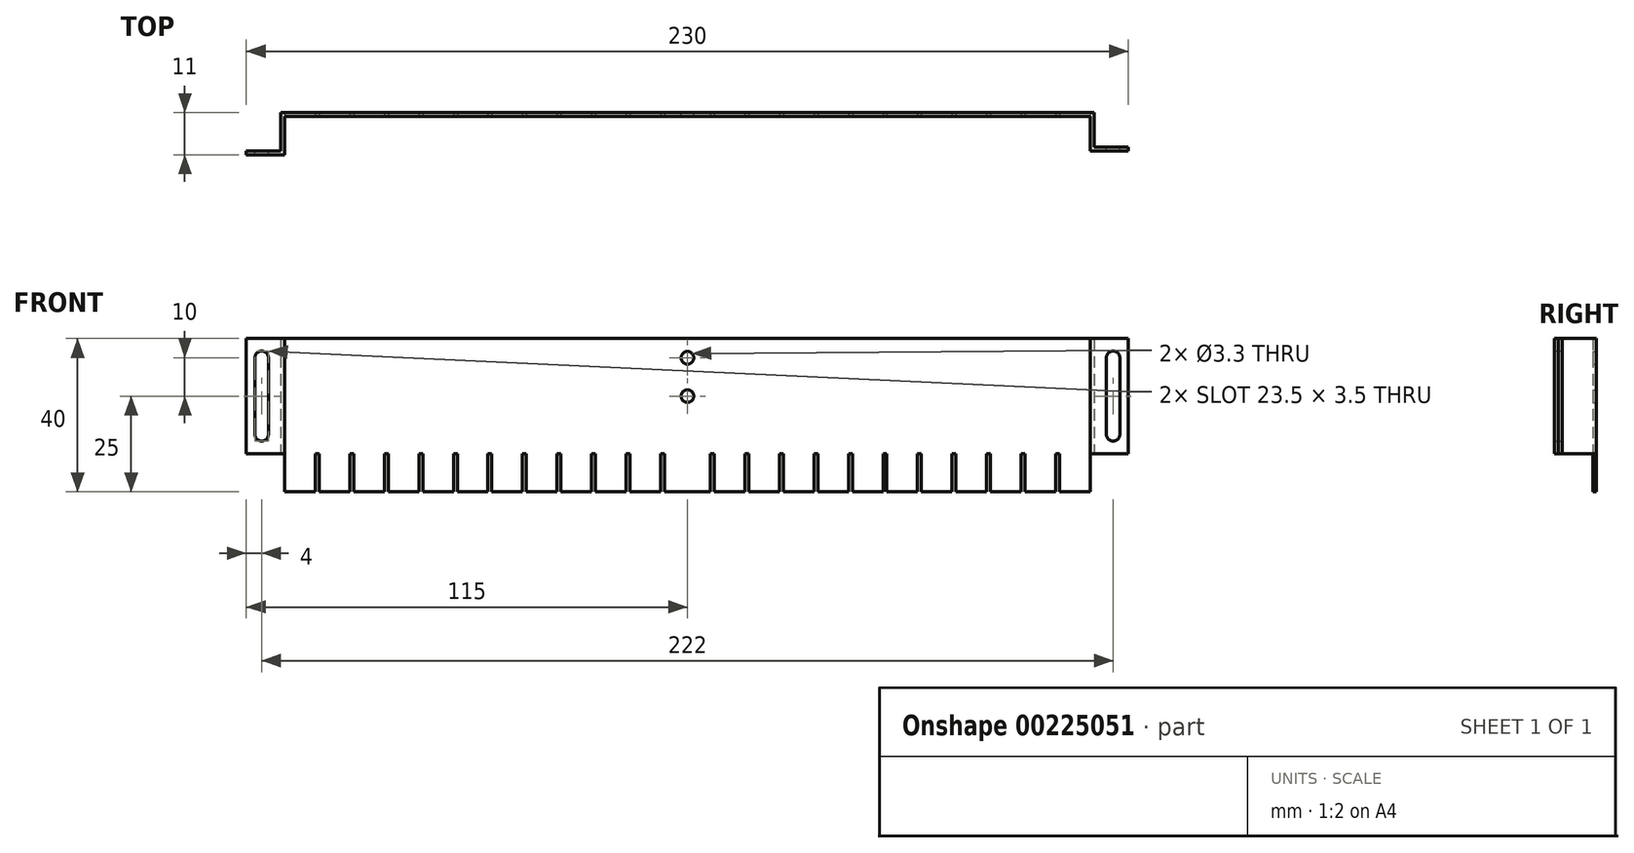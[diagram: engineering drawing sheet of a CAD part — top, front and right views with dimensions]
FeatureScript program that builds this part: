
annotation { "Feature Type Name" : "Feature", "Feature Type Description" : "" }
export const myFeature = defineFeature(function(context is Context, id is Id, definition is map)
    precondition{}
    {
        {
            var Q0;
            Q0=qCreatedBy(makeId("Top.planeOp"),FACE);
            var sketch = newSketch(context, id + "F0", { "sketchPlane" : qUnion([Q0])});
            skLineSegment(sketch, "E0", {"start": v(-115, -1) * mm, "end": v(-105, -1) * mm});
            skLineSegment(sketch, "E1", {"start": v(-105, -1) * mm, "end": v(-105, 9) * mm});
            skLineSegment(sketch, "E2", {"start": v(-105, 9) * mm, "end": v(105, 9) * mm});
            skLineSegment(sketch, "E3", {"start": v(105, 9) * mm, "end": v(105, 0) * mm});
            skLineSegment(sketch, "E4", {"start": v(105, 0) * mm, "end": v(115, 0) * mm});
            skLineSegment(sketch, "E5", {"start": v(115, 0) * mm, "end": v(115, 1) * mm});
            skLineSegment(sketch, "E6", {"start": v(115, 1) * mm, "end": v(106, 1) * mm});
            skLineSegment(sketch, "E7", {"start": v(106, 1) * mm, "end": v(106, 10) * mm});
            skLineSegment(sketch, "E8", {"start": v(106, 10) * mm, "end": v(-106, 10) * mm});
            skLineSegment(sketch, "E9", {"start": v(-106, 10) * mm, "end": v(-106, 0) * mm});
            skLineSegment(sketch, "E10", {"start": v(-106, 0) * mm, "end": v(-115, 0) * mm});
            skLineSegment(sketch, "E11", {"start": v(-115, 0) * mm, "end": v(-115, -1) * mm});
            skSolve(sketch);
        }
        {
            var Q0;
            Q0=qSketchRegion(id+"F0",true);
            extrude(context, id + "F1", {"entities" : qUnion([Q0]), "depth" : 30 * mm});
        }
        {
            var Q0;
            Q0=makeQuery(id+"F1.opExtrude","SWEPT_FACE",FACE,{"disambiguationData":[OSD([sQuery(id+"F0.wireOp",EDGE,"E6")])]});
            var sketch = newSketch(context, id + "F2", { "sketchPlane" : qUnion([Q0])});
            skArc(sketch, "E12", {"start": v(-109.25, 25) * mm, "mid": v(-111, 26.75) * mm, "end": v(-112.75, 25) * mm});
            skArc(sketch, "E13", {"start": v(-112.75, 5) * mm, "mid": v(-111, 3.25) * mm, "end": v(-109.25, 5) * mm});
            skLineSegment(sketch, "E14", {"start": v(-112.75, 25) * mm, "end": v(-112.75, 5) * mm});
            skLineSegment(sketch, "E15", {"start": v(-109.25, 5) * mm, "end": v(-109.25, 25) * mm});
            skLineSegment(sketch, "E16.MirrorCS", {"start": v(109.25, 5) * mm, "end": v(109.25, 25) * mm});
            skLineSegment(sketch, "E17.MirrorCS", {"start": v(112.75, 25) * mm, "end": v(112.75, 5) * mm});
            skArc(sketch, "E18.MirrorCS", {"start": v(112.75, 5) * mm, "mid": v(111, 3.25) * mm, "end": v(109.25, 5) * mm});
            skArc(sketch, "E19.MirrorCS", {"start": v(109.25, 25) * mm, "mid": v(111, 26.75) * mm, "end": v(112.75, 25) * mm});
            skSolve(sketch);
        }
        {
            var Q0;
            Q0=qSketchRegion(id+"F2",true);
            extrude(context, id + "F3", {"entities" : qUnion([Q0]), "operationType" : NewBodyOperationType.REMOVE, "oppositeDirection" : true, "depth" : 25 * mm});
        }
        {
            var Q0;
            Q0=makeQuery(id+"F1.opExtrude","SWEPT_FACE",FACE,{"disambiguationData":[OSD([sQuery(id+"F0.wireOp",EDGE,"E2")])]});
            var sketch = newSketch(context, id + "F4", { "sketchPlane" : qUnion([Q0])});
            skLineSegment(sketch, "E20.bottom", {"start": v(-105, 0) * mm, "end": v(-97, 0) * mm});
            skLineSegment(sketch, "E20.top", {"start": v(-105, -10) * mm, "end": v(-97, -10) * mm});
            skLineSegment(sketch, "E20.left", {"start": v(-105, 0) * mm, "end": v(-105, -10) * mm});
            skLineSegment(sketch, "E20.right", {"start": v(-97, 0) * mm, "end": v(-97, -10) * mm});
            skLineSegment(sketch, "E21.1.0.0", {"start": v(-96, 0) * mm, "end": v(-88, 0) * mm});
            skLineSegment(sketch, "E21.1.0.1", {"start": v(-96, -10) * mm, "end": v(-88, -10) * mm});
            skLineSegment(sketch, "E21.1.0.2", {"start": v(-96, 0) * mm, "end": v(-96, -10) * mm});
            skLineSegment(sketch, "E21.1.0.3", {"start": v(-88, 0) * mm, "end": v(-88, -10) * mm});
            skLineSegment(sketch, "E21.2.0.0", {"start": v(-87, 0) * mm, "end": v(-79, 0) * mm});
            skLineSegment(sketch, "E21.2.0.1", {"start": v(-87, -10) * mm, "end": v(-79, -10) * mm});
            skLineSegment(sketch, "E21.2.0.2", {"start": v(-87, 0) * mm, "end": v(-87, -10) * mm});
            skLineSegment(sketch, "E21.2.0.3", {"start": v(-79, 0) * mm, "end": v(-79, -10) * mm});
            skLineSegment(sketch, "E21.3.0.0", {"start": v(-78, 0) * mm, "end": v(-70, 0) * mm});
            skLineSegment(sketch, "E21.3.0.1", {"start": v(-78, -10) * mm, "end": v(-70, -10) * mm});
            skLineSegment(sketch, "E21.3.0.2", {"start": v(-78, 0) * mm, "end": v(-78, -10) * mm});
            skLineSegment(sketch, "E21.3.0.3", {"start": v(-70, 0) * mm, "end": v(-70, -10) * mm});
            skLineSegment(sketch, "E21.4.0.0", {"start": v(-69, 0) * mm, "end": v(-61, 0) * mm});
            skLineSegment(sketch, "E21.4.0.1", {"start": v(-69, -10) * mm, "end": v(-61, -10) * mm});
            skLineSegment(sketch, "E21.4.0.2", {"start": v(-69, 0) * mm, "end": v(-69, -10) * mm});
            skLineSegment(sketch, "E21.4.0.3", {"start": v(-61, 0) * mm, "end": v(-61, -10) * mm});
            skLineSegment(sketch, "E21.5.0.0", {"start": v(-60, 0) * mm, "end": v(-52, 0) * mm});
            skLineSegment(sketch, "E21.5.0.1", {"start": v(-60, -10) * mm, "end": v(-52, -10) * mm});
            skLineSegment(sketch, "E21.5.0.2", {"start": v(-60, 0) * mm, "end": v(-60, -10) * mm});
            skLineSegment(sketch, "E21.5.0.3", {"start": v(-52, 0) * mm, "end": v(-52, -10) * mm});
            skLineSegment(sketch, "E21.direction1", {"start": v(-105, -10) * mm, "end": v(-96, -10) * mm, "construction": true});
            skLineSegment(sketch, "E22.0.6.0", {"start": v(-51, 0) * mm, "end": v(-43, 0) * mm});
            skLineSegment(sketch, "E22.3.6.0", {"start": v(-51, -10) * mm, "end": v(-43, -10) * mm});
            skLineSegment(sketch, "E22.6.6.0", {"start": v(-51, 0) * mm, "end": v(-51, -10) * mm});
            skLineSegment(sketch, "E22.9.6.0", {"start": v(-43, 0) * mm, "end": v(-43, -10) * mm});
            skLineSegment(sketch, "E22.0.7.0", {"start": v(-42, 0) * mm, "end": v(-34, 0) * mm});
            skLineSegment(sketch, "E22.3.7.0", {"start": v(-42, -10) * mm, "end": v(-34, -10) * mm});
            skLineSegment(sketch, "E22.6.7.0", {"start": v(-42, 0) * mm, "end": v(-42, -10) * mm});
            skLineSegment(sketch, "E22.9.7.0", {"start": v(-34, 0) * mm, "end": v(-34, -10) * mm});
            skLineSegment(sketch, "E22.0.8.0", {"start": v(-33, 0) * mm, "end": v(-25, 0) * mm});
            skLineSegment(sketch, "E22.3.8.0", {"start": v(-33, -10) * mm, "end": v(-25, -10) * mm});
            skLineSegment(sketch, "E22.6.8.0", {"start": v(-33, 0) * mm, "end": v(-33, -10) * mm});
            skLineSegment(sketch, "E22.9.8.0", {"start": v(-25, 0) * mm, "end": v(-25, -10) * mm});
            skLineSegment(sketch, "E22.0.9.0", {"start": v(-24, 0) * mm, "end": v(-16, 0) * mm});
            skLineSegment(sketch, "E22.3.9.0", {"start": v(-24, -10) * mm, "end": v(-16, -10) * mm});
            skLineSegment(sketch, "E22.6.9.0", {"start": v(-24, 0) * mm, "end": v(-24, -10) * mm});
            skLineSegment(sketch, "E22.9.9.0", {"start": v(-16, 0) * mm, "end": v(-16, -10) * mm});
            skLineSegment(sketch, "E23.0.10.0", {"start": v(-15, 0) * mm, "end": v(-7, 0) * mm});
            skLineSegment(sketch, "E23.3.10.0", {"start": v(-15, -10) * mm, "end": v(-7, -10) * mm});
            skLineSegment(sketch, "E23.6.10.0", {"start": v(-15, 0) * mm, "end": v(-15, -10) * mm});
            skLineSegment(sketch, "E23.9.10.0", {"start": v(-7, 0) * mm, "end": v(-7, -10) * mm});
            skPoint(sketch, "E24.oppositeSnap0", {"position": v(-100.5, -10) * mm});
            skLineSegment(sketch, "E24.bottom", {"start": v(105, 0) * mm, "end": v(97, 0) * mm});
            skLineSegment(sketch, "E24.top", {"start": v(105, -10) * mm, "end": v(97, -10) * mm});
            skLineSegment(sketch, "E24.left", {"start": v(105, 0) * mm, "end": v(105, -10) * mm});
            skLineSegment(sketch, "E24.right", {"start": v(97, 0) * mm, "end": v(97, -10) * mm});
            skLineSegment(sketch, "E25.1.0.0", {"start": v(96, -10) * mm, "end": v(88, -10) * mm});
            skLineSegment(sketch, "E25.1.0.1", {"start": v(96, 0) * mm, "end": v(88, 0) * mm});
            skLineSegment(sketch, "E25.1.0.2", {"start": v(88, 0) * mm, "end": v(88, -10) * mm});
            skLineSegment(sketch, "E25.1.0.3", {"start": v(96, 0) * mm, "end": v(96, -10) * mm});
            skLineSegment(sketch, "E25.2.0.0", {"start": v(87, -10) * mm, "end": v(79, -10) * mm});
            skLineSegment(sketch, "E25.2.0.1", {"start": v(87, 0) * mm, "end": v(79, 0) * mm});
            skLineSegment(sketch, "E25.2.0.2", {"start": v(79, 0) * mm, "end": v(79, -10) * mm});
            skLineSegment(sketch, "E25.2.0.3", {"start": v(87, 0) * mm, "end": v(87, -10) * mm});
            skLineSegment(sketch, "E25.3.0.0", {"start": v(78, -10) * mm, "end": v(70, -10) * mm});
            skLineSegment(sketch, "E25.3.0.1", {"start": v(78, 0) * mm, "end": v(70, 0) * mm});
            skLineSegment(sketch, "E25.3.0.2", {"start": v(70, 0) * mm, "end": v(70, -10) * mm});
            skLineSegment(sketch, "E25.3.0.3", {"start": v(78, 0) * mm, "end": v(78, -10) * mm});
            skLineSegment(sketch, "E25.4.0.0", {"start": v(69, -10) * mm, "end": v(61, -10) * mm});
            skLineSegment(sketch, "E25.4.0.1", {"start": v(69, 0) * mm, "end": v(61, 0) * mm});
            skLineSegment(sketch, "E25.4.0.2", {"start": v(61, 0) * mm, "end": v(61, -10) * mm});
            skLineSegment(sketch, "E25.4.0.3", {"start": v(69, 0) * mm, "end": v(69, -10) * mm});
            skLineSegment(sketch, "E25.5.0.0", {"start": v(60, -10) * mm, "end": v(52, -10) * mm});
            skLineSegment(sketch, "E25.5.0.1", {"start": v(60, 0) * mm, "end": v(52, 0) * mm});
            skLineSegment(sketch, "E25.5.0.2", {"start": v(52, 0) * mm, "end": v(52, -10) * mm});
            skLineSegment(sketch, "E25.5.0.3", {"start": v(60, 0) * mm, "end": v(60, -10) * mm});
            skLineSegment(sketch, "E25.6.0.0", {"start": v(51, -10) * mm, "end": v(43, -10) * mm});
            skLineSegment(sketch, "E25.6.0.1", {"start": v(51, 0) * mm, "end": v(43, 0) * mm});
            skLineSegment(sketch, "E25.6.0.2", {"start": v(43, 0) * mm, "end": v(43, -10) * mm});
            skLineSegment(sketch, "E25.6.0.3", {"start": v(51, 0) * mm, "end": v(51, -10) * mm});
            skLineSegment(sketch, "E25.7.0.0", {"start": v(42, -10) * mm, "end": v(34, -10) * mm});
            skLineSegment(sketch, "E25.7.0.1", {"start": v(42, 0) * mm, "end": v(34, 0) * mm});
            skLineSegment(sketch, "E25.7.0.2", {"start": v(34, 0) * mm, "end": v(34, -10) * mm});
            skLineSegment(sketch, "E25.7.0.3", {"start": v(42, 0) * mm, "end": v(42, -10) * mm});
            skLineSegment(sketch, "E25.8.0.0", {"start": v(33, -10) * mm, "end": v(25, -10) * mm});
            skLineSegment(sketch, "E25.8.0.1", {"start": v(33, 0) * mm, "end": v(25, 0) * mm});
            skLineSegment(sketch, "E25.8.0.2", {"start": v(25, 0) * mm, "end": v(25, -10) * mm});
            skLineSegment(sketch, "E25.8.0.3", {"start": v(33, 0) * mm, "end": v(33, -10) * mm});
            skLineSegment(sketch, "E25.9.0.0", {"start": v(24, -10) * mm, "end": v(16, -10) * mm});
            skLineSegment(sketch, "E25.9.0.1", {"start": v(24, 0) * mm, "end": v(16, 0) * mm});
            skLineSegment(sketch, "E25.9.0.2", {"start": v(16, 0) * mm, "end": v(16, -10) * mm});
            skLineSegment(sketch, "E25.9.0.3", {"start": v(24, 0) * mm, "end": v(24, -10) * mm});
            skLineSegment(sketch, "E25.10.0.0", {"start": v(15, -10) * mm, "end": v(7, -10) * mm});
            skLineSegment(sketch, "E25.10.0.1", {"start": v(15, 0) * mm, "end": v(7, 0) * mm});
            skLineSegment(sketch, "E25.10.0.2", {"start": v(7, 0) * mm, "end": v(7, -10) * mm});
            skLineSegment(sketch, "E25.10.0.3", {"start": v(15, 0) * mm, "end": v(15, -10) * mm});
            skLineSegment(sketch, "E25.direction1", {"start": v(97, -10) * mm, "end": v(88, -10) * mm, "construction": true});
            skLineSegment(sketch, "E26.bottom", {"start": v(6, 0) * mm, "end": v(-6, 0) * mm});
            skLineSegment(sketch, "E26.top", {"start": v(6, -10) * mm, "end": v(-6, -10) * mm});
            skLineSegment(sketch, "E26.left", {"start": v(6, 0) * mm, "end": v(6, -10) * mm});
            skLineSegment(sketch, "E26.right", {"start": v(-6, 0) * mm, "end": v(-6, -10) * mm});
            skSolve(sketch);
        }
        {
            var Q0;
            Q0 = qSketchRegion(id + "F4", true);
            extrude(context, id + "F5", {"entities" : qUnion([Q0]), "operationType" : NewBodyOperationType.ADD, "oppositeDirection" : true, "depth" : 1 * mm});
        }
        {
            var Q0;
            Q0=makeQuery(id+"F5.boolean.opBoolean","MERGE",FACE,{"derivedFrom":[makeQuery(id+"F1.opExtrude","SWEPT_FACE",FACE,{"disambiguationData":[OSD([sQuery(id+"F0.wireOp",EDGE,"E8")])]}),makeQuery(id+"F5.opExtrude","CAP_FACE",FACE,{"disambiguationData":[OSD([sQuery(id+"F4.wireOp",EDGE,"E20.bottom"),sQuery(id+"F4.wireOp",EDGE,"E20.top"),sQuery(id+"F4.wireOp",EDGE,"E20.left"),sQuery(id+"F4.wireOp",EDGE,"E20.right")])],"isStart":false}),makeQuery(id+"F5.opExtrude","CAP_FACE",FACE,{"disambiguationData":[OSD([sQuery(id+"F4.wireOp",EDGE,"E21.1.0.0"),sQuery(id+"F4.wireOp",EDGE,"E21.1.0.1"),sQuery(id+"F4.wireOp",EDGE,"E21.1.0.2"),sQuery(id+"F4.wireOp",EDGE,"E21.1.0.3")])],"isStart":false}),makeQuery(id+"F5.opExtrude","CAP_FACE",FACE,{"disambiguationData":[OSD([sQuery(id+"F4.wireOp",EDGE,"E21.2.0.0"),sQuery(id+"F4.wireOp",EDGE,"E21.2.0.1"),sQuery(id+"F4.wireOp",EDGE,"E21.2.0.2"),sQuery(id+"F4.wireOp",EDGE,"E21.2.0.3")])],"isStart":false}),makeQuery(id+"F5.opExtrude","CAP_FACE",FACE,{"disambiguationData":[OSD([sQuery(id+"F4.wireOp",EDGE,"E21.3.0.0"),sQuery(id+"F4.wireOp",EDGE,"E21.3.0.1"),sQuery(id+"F4.wireOp",EDGE,"E21.3.0.2"),sQuery(id+"F4.wireOp",EDGE,"E21.3.0.3")])],"isStart":false}),makeQuery(id+"F5.opExtrude","CAP_FACE",FACE,{"disambiguationData":[OSD([sQuery(id+"F4.wireOp",EDGE,"E21.4.0.0"),sQuery(id+"F4.wireOp",EDGE,"E21.4.0.1"),sQuery(id+"F4.wireOp",EDGE,"E21.4.0.2"),sQuery(id+"F4.wireOp",EDGE,"E21.4.0.3")])],"isStart":false}),makeQuery(id+"F5.opExtrude","CAP_FACE",FACE,{"disambiguationData":[OSD([sQuery(id+"F4.wireOp",EDGE,"E21.5.0.0"),sQuery(id+"F4.wireOp",EDGE,"E21.5.0.1"),sQuery(id+"F4.wireOp",EDGE,"E21.5.0.2"),sQuery(id+"F4.wireOp",EDGE,"E21.5.0.3")])],"isStart":false}),makeQuery(id+"F5.opExtrude","CAP_FACE",FACE,{"disambiguationData":[OSD([sQuery(id+"F4.wireOp",EDGE,"E21.6.0.0"),sQuery(id+"F4.wireOp",EDGE,"E21.6.0.1"),sQuery(id+"F4.wireOp",EDGE,"E21.6.0.2"),sQuery(id+"F4.wireOp",EDGE,"E21.6.0.3")])],"isStart":false}),makeQuery(id+"F5.opExtrude","CAP_FACE",FACE,{"disambiguationData":[OSD([sQuery(id+"F4.wireOp",EDGE,"E21.7.0.0"),sQuery(id+"F4.wireOp",EDGE,"E21.7.0.1"),sQuery(id+"F4.wireOp",EDGE,"E21.7.0.2"),sQuery(id+"F4.wireOp",EDGE,"E21.7.0.3")])],"isStart":false}),makeQuery(id+"F5.opExtrude","CAP_FACE",FACE,{"disambiguationData":[OSD([sQuery(id+"F4.wireOp",EDGE,"E21.8.0.0"),sQuery(id+"F4.wireOp",EDGE,"E21.8.0.1"),sQuery(id+"F4.wireOp",EDGE,"E21.8.0.2"),sQuery(id+"F4.wireOp",EDGE,"E21.8.0.3")])],"isStart":false}),makeQuery(id+"F5.opExtrude","CAP_FACE",FACE,{"disambiguationData":[OSD([sQuery(id+"F4.wireOp",EDGE,"E21.9.0.0"),sQuery(id+"F4.wireOp",EDGE,"E21.9.0.1"),sQuery(id+"F4.wireOp",EDGE,"E21.9.0.2"),sQuery(id+"F4.wireOp",EDGE,"E21.9.0.3")])],"isStart":false}),makeQuery(id+"F5.opExtrude","CAP_FACE",FACE,{"disambiguationData":[OSD([sQuery(id+"F4.wireOp",EDGE,"E21.10.0.0"),sQuery(id+"F4.wireOp",EDGE,"E21.10.0.1"),sQuery(id+"F4.wireOp",EDGE,"E21.10.0.2"),sQuery(id+"F4.wireOp",EDGE,"E21.10.0.3")])],"isStart":false}),makeQuery(id+"F5.opExtrude","CAP_FACE",FACE,{"disambiguationData":[OSD([sQuery(id+"F4.wireOp",EDGE,"E21.11.0.0"),sQuery(id+"F4.wireOp",EDGE,"E21.11.0.1"),sQuery(id+"F4.wireOp",EDGE,"E21.11.0.2"),sQuery(id+"F4.wireOp",EDGE,"E21.11.0.3")])],"isStart":false}),makeQuery(id+"F5.opExtrude","CAP_FACE",FACE,{"disambiguationData":[OSD([sQuery(id+"F4.wireOp",EDGE,"E21.12.0.0"),sQuery(id+"F4.wireOp",EDGE,"E21.12.0.1"),sQuery(id+"F4.wireOp",EDGE,"E21.12.0.2"),sQuery(id+"F4.wireOp",EDGE,"E21.12.0.3")])],"isStart":false}),makeQuery(id+"F5.opExtrude","CAP_FACE",FACE,{"disambiguationData":[OSD([sQuery(id+"F4.wireOp",EDGE,"E21.13.0.0"),sQuery(id+"F4.wireOp",EDGE,"E21.13.0.1"),sQuery(id+"F4.wireOp",EDGE,"E21.13.0.2"),sQuery(id+"F4.wireOp",EDGE,"E21.13.0.3")])],"isStart":false}),makeQuery(id+"F5.opExtrude","CAP_FACE",FACE,{"disambiguationData":[OSD([sQuery(id+"F4.wireOp",EDGE,"E21.14.0.0"),sQuery(id+"F4.wireOp",EDGE,"E21.14.0.1"),sQuery(id+"F4.wireOp",EDGE,"E21.14.0.2"),sQuery(id+"F4.wireOp",EDGE,"E21.14.0.3")])],"isStart":false}),makeQuery(id+"F5.opExtrude","CAP_FACE",FACE,{"disambiguationData":[OSD([sQuery(id+"F4.wireOp",EDGE,"E21.15.0.0"),sQuery(id+"F4.wireOp",EDGE,"E21.15.0.1"),sQuery(id+"F4.wireOp",EDGE,"E21.15.0.2"),sQuery(id+"F4.wireOp",EDGE,"E21.15.0.3")])],"isStart":false}),makeQuery(id+"F5.opExtrude","CAP_FACE",FACE,{"disambiguationData":[OSD([sQuery(id+"F4.wireOp",EDGE,"E21.16.0.0"),sQuery(id+"F4.wireOp",EDGE,"E21.16.0.1"),sQuery(id+"F4.wireOp",EDGE,"E21.16.0.2"),sQuery(id+"F4.wireOp",EDGE,"E21.16.0.3")])],"isStart":false}),makeQuery(id+"F5.opExtrude","CAP_FACE",FACE,{"disambiguationData":[OSD([sQuery(id+"F4.wireOp",EDGE,"E21.17.0.0"),sQuery(id+"F4.wireOp",EDGE,"E21.17.0.1"),sQuery(id+"F4.wireOp",EDGE,"E21.17.0.2"),sQuery(id+"F4.wireOp",EDGE,"E21.17.0.3")])],"isStart":false}),makeQuery(id+"F5.opExtrude","CAP_FACE",FACE,{"disambiguationData":[OSD([sQuery(id+"F4.wireOp",EDGE,"E21.18.0.0"),sQuery(id+"F4.wireOp",EDGE,"E21.18.0.1"),sQuery(id+"F4.wireOp",EDGE,"E21.18.0.2"),sQuery(id+"F4.wireOp",EDGE,"E21.18.0.3")])],"isStart":false}),makeQuery(id+"F5.opExtrude","CAP_FACE",FACE,{"disambiguationData":[OSD([sQuery(id+"F4.wireOp",EDGE,"E21.19.0.0"),sQuery(id+"F4.wireOp",EDGE,"E21.19.0.1"),sQuery(id+"F4.wireOp",EDGE,"E21.19.0.2"),sQuery(id+"F4.wireOp",EDGE,"E21.19.0.3")])],"isStart":false}),makeQuery(id+"F5.opExtrude","CAP_FACE",FACE,{"disambiguationData":[OSD([sQuery(id+"F4.wireOp",EDGE,"E21.20.0.0"),sQuery(id+"F4.wireOp",EDGE,"E21.20.0.1"),sQuery(id+"F4.wireOp",EDGE,"E21.20.0.2"),sQuery(id+"F4.wireOp",EDGE,"E21.20.0.3")])],"isStart":false}),makeQuery(id+"F5.opExtrude","CAP_FACE",FACE,{"disambiguationData":[OSD([sQuery(id+"F4.wireOp",EDGE,"E21.21.0.0"),sQuery(id+"F4.wireOp",EDGE,"E21.21.0.1"),sQuery(id+"F4.wireOp",EDGE,"E21.21.0.2"),sQuery(id+"F4.wireOp",EDGE,"E21.21.0.3")])],"isStart":false}),makeQuery(id+"F5.opExtrude","CAP_FACE",FACE,{"disambiguationData":[OSD([sQuery(id+"F4.wireOp",EDGE,"E21.22.0.0"),sQuery(id+"F4.wireOp",EDGE,"E21.22.0.1"),sQuery(id+"F4.wireOp",EDGE,"E21.22.0.2"),sQuery(id+"F4.wireOp",EDGE,"E21.22.0.3")])],"isStart":false}),makeQuery(id+"F5.opExtrude","CAP_FACE",FACE,{"disambiguationData":[OSD([sQuery(id+"F4.wireOp",EDGE,"E21.23.0.0"),sQuery(id+"F4.wireOp",EDGE,"E21.23.0.1"),sQuery(id+"F4.wireOp",EDGE,"E21.23.0.2"),sQuery(id+"F4.wireOp",EDGE,"E21.23.0.3")])],"isStart":false}),makeQuery(id+"F5.opExtrude","CAP_FACE",FACE,{"disambiguationData":[OSD([sQuery(id+"F4.wireOp",EDGE,"80ee39f5-79b0-4ce6-8144-c18897430cea.0.24.0"),sQuery(id+"F4.wireOp",EDGE,"80ee39f5-79b0-4ce6-8144-c18897430cea.3.24.0"),sQuery(id+"F4.wireOp",EDGE,"80ee39f5-79b0-4ce6-8144-c18897430cea.6.24.0"),sQuery(id+"F4.wireOp",EDGE,"80ee39f5-79b0-4ce6-8144-c18897430cea.9.24.0")])],"isStart":false}),makeQuery(id+"F5.opExtrude","CAP_FACE",FACE,{"disambiguationData":[OSD([sQuery(id+"F4.wireOp",EDGE,"46cf1773-859a-4cdb-9547-5b81ae7c1765.0.25.0"),sQuery(id+"F4.wireOp",EDGE,"46cf1773-859a-4cdb-9547-5b81ae7c1765.3.25.0"),sQuery(id+"F4.wireOp",EDGE,"46cf1773-859a-4cdb-9547-5b81ae7c1765.6.25.0"),sQuery(id+"F4.wireOp",EDGE,"46cf1773-859a-4cdb-9547-5b81ae7c1765.9.25.0")])],"isStart":false})]});
            var sketch = newSketch(context, id + "F6", { "sketchPlane" : qUnion([Q0])});
            skPoint(sketch, "E27", {"position": v(0, 25) * mm});
            skPoint(sketch, "E28", {"position": v(0, 15) * mm});
            skSolve(sketch);
        }
        {
            var Q0;
            Q0=sQuery(id+"F6.wireOp",VERTEX,"E28");
            var Q1;
            Q1=sQuery(id+"F6.wireOp",VERTEX,"E27");
            var Q2;
            Q2=makeQuery(id+"F1.opExtrude","SWEPT_BODY",BODY,{"disambiguationData":[OSD([sQuery(id+"F0.wireOp",EDGE,"E0"),sQuery(id+"F0.wireOp",EDGE,"E1"),sQuery(id+"F0.wireOp",EDGE,"E2"),sQuery(id+"F0.wireOp",EDGE,"E3"),sQuery(id+"F0.wireOp",EDGE,"E4"),sQuery(id+"F0.wireOp",EDGE,"E5"),sQuery(id+"F0.wireOp",EDGE,"E6"),sQuery(id+"F0.wireOp",EDGE,"E7"),sQuery(id+"F0.wireOp",EDGE,"E8"),sQuery(id+"F0.wireOp",EDGE,"E9"),sQuery(id+"F0.wireOp",EDGE,"E10"),sQuery(id+"F0.wireOp",EDGE,"E11")])]});
            hole(context, id + "F7", {"style" : HoleStyle.SIMPLE, "endStyle" : HoleEndStyle.THROUGH, "standardTappedOrClearance" : lookupTablePath({ "standard" : "ISO", "fit" : "Normal", "size" : "M3", "type" : "Clearance" }), "standardBlindInLast" : lookupTablePath({ "fit" : "Standard", "standard" : "ISO", "size" : "M3", "type" : "Clearance" }), "holeDiameter" : 3.3 * mm, "tappedDepth" : 12 * mm, "tapClearance" : 3, "locations" : qUnion([Q0, Q1]), "scope" : qUnion([Q2])});
        }
    });
